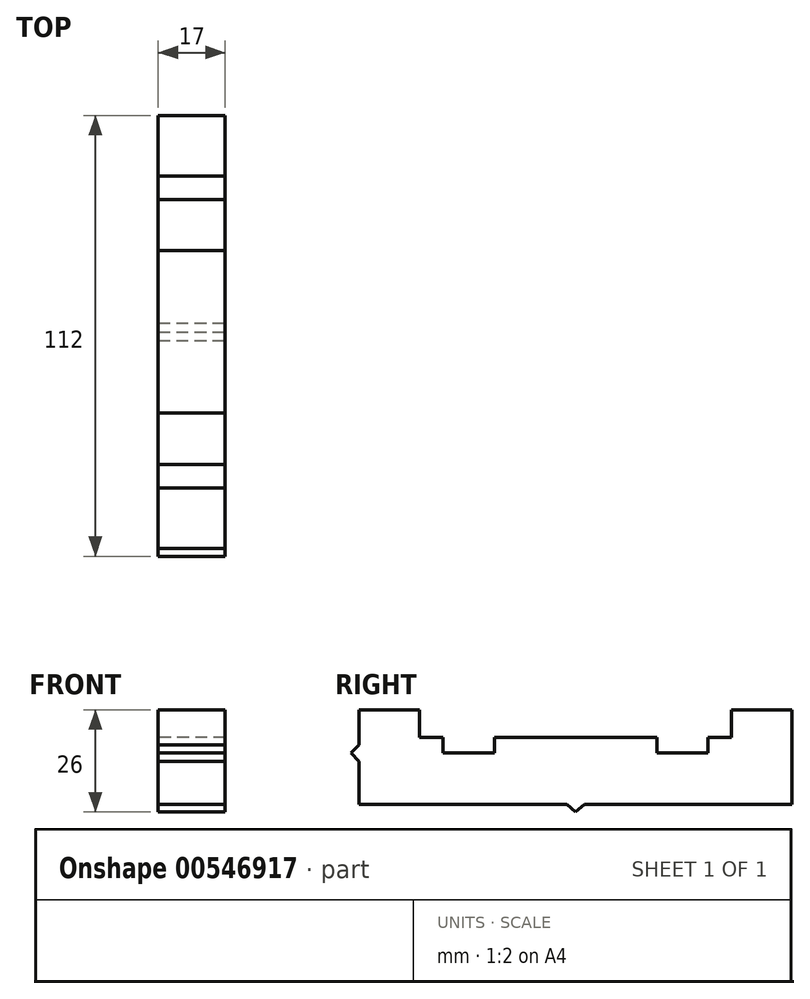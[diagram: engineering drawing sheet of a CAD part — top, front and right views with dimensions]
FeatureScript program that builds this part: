
annotation { "Feature Type Name" : "Feature", "Feature Type Description" : "" }
export const myFeature = defineFeature(function(context is Context, id is Id, definition is map)
    precondition{}
    {
        {
            var Q0;
            Q0=qCreatedBy(makeId("Right.planeOp"),FACE);
            var sketch = newSketch(context, id + "F0", { "sketchPlane" : qUnion([Q0])});
            skLineSegment(sketch, "E0.bottom", {"start": v(0, 0) * mm, "end": v(110, 0) * mm});
            skLineSegment(sketch, "E0.top", {"start": v(0, 24) * mm, "end": v(110, 24) * mm});
            skLineSegment(sketch, "E0.left", {"start": v(0, 0) * mm, "end": v(0, 24) * mm});
            skLineSegment(sketch, "E0.right", {"start": v(110, 0) * mm, "end": v(110, 24) * mm});
            skLineSegment(sketch, "E1.bottom", {"start": v(15.35, 24) * mm, "end": v(94.65, 24) * mm});
            skLineSegment(sketch, "E1.top", {"start": v(15.35, 17) * mm, "end": v(94.65, 17) * mm, "construction": true});
            skLineSegment(sketch, "E1.left", {"start": v(15.35, 24) * mm, "end": v(15.35, 17) * mm});
            skLineSegment(sketch, "E1.right", {"start": v(94.65, 24) * mm, "end": v(94.65, 17) * mm});
            skLineSegment(sketch, "E2", {"start": v(55, 24) * mm, "end": v(55, 0) * mm, "construction": true});
            skLineSegment(sketch, "E3.bottom", {"start": v(21.35, 17) * mm, "end": v(34.35, 17) * mm});
            skLineSegment(sketch, "E3.top", {"start": v(21.35, 13) * mm, "end": v(34.35, 13) * mm});
            skLineSegment(sketch, "E3.left", {"start": v(21.35, 17) * mm, "end": v(21.35, 13) * mm});
            skLineSegment(sketch, "E3.right", {"start": v(34.35, 17) * mm, "end": v(34.35, 13) * mm});
            skLineSegment(sketch, "E4.bottom", {"start": v(88.65, 17) * mm, "end": v(75.65, 17) * mm});
            skLineSegment(sketch, "E4.top", {"start": v(88.65, 13) * mm, "end": v(75.65, 13) * mm});
            skLineSegment(sketch, "E4.left", {"start": v(88.65, 17) * mm, "end": v(88.65, 13) * mm});
            skLineSegment(sketch, "E4.right", {"start": v(75.65, 17) * mm, "end": v(75.65, 13) * mm});
            skLineSegment(sketch, "E5", {"start": v(15.35, 17) * mm, "end": v(21.35, 17) * mm, "construction": true});
            skLineSegment(sketch, "E6", {"start": v(15.35, 17) * mm, "end": v(21.35, 17) * mm});
            skLineSegment(sketch, "E7", {"start": v(34.35, 17) * mm, "end": v(75.65, 17) * mm});
            skLineSegment(sketch, "E8", {"start": v(88.65, 17) * mm, "end": v(94.65, 17) * mm});
            skSolve(sketch);
        }
        {
            var Q0;
            Q0=makeQuery(id+"F0.imprint","IMPRINT",FACE,{"disambiguationData":[TD([[makeQuery(id+"F0.imprint","IMPRINT",EDGE,{"derivedFrom":sQuery(id+"F0.wireOp",EDGE,"E0.bottom")}),1.0]])]});
            extrude(context, id + "F1", {"entities" : qUnion([Q0]), "depth" : 17 * mm, "offsetDistance" : 25 * mm});
        }
        {
            var Q0;
            Q0=makeQuery(id+"F1.opExtrude","CAP_FACE",FACE,{"disambiguationData":[OSD([sQuery(id+"F0.wireOp",EDGE,"E0.bottom"),sQuery(id+"F0.wireOp",EDGE,"E0.top"),sQuery(id+"F0.wireOp",EDGE,"E0.left"),sQuery(id+"F0.wireOp",EDGE,"E0.right"),sQuery(id+"F0.wireOp",EDGE,"E1.left"),sQuery(id+"F0.wireOp",EDGE,"E1.right"),sQuery(id+"F0.wireOp",EDGE,"E3.top"),sQuery(id+"F0.wireOp",EDGE,"E3.left"),sQuery(id+"F0.wireOp",EDGE,"E3.right"),sQuery(id+"F0.wireOp",EDGE,"E4.top"),sQuery(id+"F0.wireOp",EDGE,"E4.left"),sQuery(id+"F0.wireOp",EDGE,"E4.right"),sQuery(id+"F0.wireOp",EDGE,"E6"),sQuery(id+"F0.wireOp",EDGE,"E7"),sQuery(id+"F0.wireOp",EDGE,"E8")])],"isStart":false});
            var sketch = newSketch(context, id + "F2", { "sketchPlane" : qUnion([Q0])});
            skLineSegment(sketch, "E9.0", {"start": v(0, 0) * mm, "end": v(110, 0) * mm});
            skLineSegment(sketch, "E10", {"start": v(55, 0) * mm, "end": v(55, -2) * mm});
            skLineSegment(sketch, "E11", {"start": v(55, -2) * mm, "end": v(52.76, 0) * mm});
            skLineSegment(sketch, "E12", {"start": v(52.76, 0) * mm, "end": v(55, 0) * mm});
            skLineSegment(sketch, "E13.MirrorCS", {"start": v(55, -2) * mm, "end": v(57.24, 0) * mm});
            skLineSegment(sketch, "E14.MirrorCS", {"start": v(57.24, 0) * mm, "end": v(55, 0) * mm});
            skSolve(sketch);
        }
        {
            var Q0;
            Q0=makeQuery(id+"F2.imprint","IMPRINT",FACE,{"disambiguationData":[TD([[makeQuery(id+"F2.imprint","IMPRINT",EDGE,{"derivedFrom":sQuery(id+"F2.wireOp",EDGE,"E10")}),1.0]])]});
            var Q1;
            Q1=makeQuery(id+"F2.imprint","IMPRINT",FACE,{"disambiguationData":[TD([[makeQuery(id+"F2.imprint","IMPRINT",EDGE,{"derivedFrom":sQuery(id+"F2.wireOp",EDGE,"E10")}),-1.0]])]});
            var Q2;
            Q2=makeQuery(id+"F1.opExtrude","CAP_FACE",FACE,{"disambiguationData":[OSD([sQuery(id+"F0.wireOp",EDGE,"E0.bottom"),sQuery(id+"F0.wireOp",EDGE,"E0.top"),sQuery(id+"F0.wireOp",EDGE,"E0.left"),sQuery(id+"F0.wireOp",EDGE,"E0.right"),sQuery(id+"F0.wireOp",EDGE,"E1.left"),sQuery(id+"F0.wireOp",EDGE,"E1.right"),sQuery(id+"F0.wireOp",EDGE,"E3.top"),sQuery(id+"F0.wireOp",EDGE,"E3.left"),sQuery(id+"F0.wireOp",EDGE,"E3.right"),sQuery(id+"F0.wireOp",EDGE,"E4.top"),sQuery(id+"F0.wireOp",EDGE,"E4.left"),sQuery(id+"F0.wireOp",EDGE,"E4.right"),sQuery(id+"F0.wireOp",EDGE,"E6"),sQuery(id+"F0.wireOp",EDGE,"E7"),sQuery(id+"F0.wireOp",EDGE,"E8")])],"isStart":true});
            extrude(context, id + "F3", {"entities" : qUnion([Q0, Q1]), "operationType" : NewBodyOperationType.ADD, "endBound" : BoundingType.UP_TO_SURFACE, "oppositeDirection" : true, "depth" : 25 * mm, "endBoundEntityFace" : qUnion([Q2]), "offsetDistance" : 25 * mm});
        }
        {
            var Q0;
            Q0=makeQuery(id+"F3.boolean.opBoolean","MERGE",FACE,{"derivedFrom":[makeQuery(id+"F1.opExtrude","CAP_FACE",FACE,{"disambiguationData":[OSD([sQuery(id+"F0.wireOp",EDGE,"E0.bottom"),sQuery(id+"F0.wireOp",EDGE,"E0.top"),sQuery(id+"F0.wireOp",EDGE,"E0.left"),sQuery(id+"F0.wireOp",EDGE,"E0.right"),sQuery(id+"F0.wireOp",EDGE,"E1.left"),sQuery(id+"F0.wireOp",EDGE,"E1.right"),sQuery(id+"F0.wireOp",EDGE,"E3.top"),sQuery(id+"F0.wireOp",EDGE,"E3.left"),sQuery(id+"F0.wireOp",EDGE,"E3.right"),sQuery(id+"F0.wireOp",EDGE,"E4.top"),sQuery(id+"F0.wireOp",EDGE,"E4.left"),sQuery(id+"F0.wireOp",EDGE,"E4.right"),sQuery(id+"F0.wireOp",EDGE,"E6"),sQuery(id+"F0.wireOp",EDGE,"E7"),sQuery(id+"F0.wireOp",EDGE,"E8")])],"isStart":false}),makeQuery(id+"F3.opExtrude","CAP_FACE",FACE,{"disambiguationData":[OSD([sQuery(id+"F2.wireOp",EDGE,"E11"),sQuery(id+"F2.wireOp",EDGE,"E12"),sQuery(id+"F2.wireOp",EDGE,"E13.MirrorCS"),sQuery(id+"F2.wireOp",EDGE,"E14.MirrorCS")])],"isStart":true})]});
            var sketch = newSketch(context, id + "F4", { "sketchPlane" : qUnion([Q0])});
            skLineSegment(sketch, "E15.0", {"start": v(21.35, 13) * mm, "end": v(34.35, 13) * mm});
            skLineSegment(sketch, "E16", {"start": v(21.35, 13) * mm, "end": v(0, 13) * mm});
            skLineSegment(sketch, "E17", {"start": v(0, 13) * mm, "end": v(-2, 13) * mm});
            skLineSegment(sketch, "E18", {"start": v(-2, 13) * mm, "end": v(0, 15.12) * mm});
            skLineSegment(sketch, "E19", {"start": v(0, 15.12) * mm, "end": v(0, 13) * mm});
            skLineSegment(sketch, "E20.MirrorCS", {"start": v(-2, 13) * mm, "end": v(0, 10.88) * mm});
            skLineSegment(sketch, "E21.MirrorCS", {"start": v(0, 10.88) * mm, "end": v(0, 13) * mm});
            skSolve(sketch);
        }
        {
            var Q0;
            Q0=makeQuery(id+"F4.imprint","IMPRINT",FACE,{"disambiguationData":[TD([[makeQuery(id+"F4.imprint","IMPRINT",EDGE,{"derivedFrom":sQuery(id+"F4.wireOp",EDGE,"E17")}),1.0]])]});
            var Q1;
            Q1=makeQuery(id+"F4.imprint","IMPRINT",FACE,{"disambiguationData":[TD([[makeQuery(id+"F4.imprint","IMPRINT",EDGE,{"derivedFrom":sQuery(id+"F4.wireOp",EDGE,"E17")}),-1.0]])]});
            var Q2;
            {var subQ0=sQuery(id+"F0.wireOp",EDGE,"E8");var subQ1=sQuery(id+"F0.wireOp",EDGE,"E7");var subQ2=sQuery(id+"F0.wireOp",EDGE,"E6");var subQ3=sQuery(id+"F0.wireOp",EDGE,"E4.right");var subQ4=sQuery(id+"F0.wireOp",EDGE,"E4.left");var subQ5=sQuery(id+"F0.wireOp",EDGE,"E4.top");var subQ6=sQuery(id+"F0.wireOp",EDGE,"E3.right");var subQ7=sQuery(id+"F0.wireOp",EDGE,"E3.left");var subQ8=sQuery(id+"F0.wireOp",EDGE,"E3.top");var subQ9=sQuery(id+"F0.wireOp",EDGE,"E1.right");var subQ10=sQuery(id+"F0.wireOp",EDGE,"E1.left");var subQ11=sQuery(id+"F0.wireOp",EDGE,"E0.right");var subQ12=sQuery(id+"F0.wireOp",EDGE,"E0.left");var subQ13=sQuery(id+"F0.wireOp",EDGE,"E0.top");var subQ14=sQuery(id+"F0.wireOp",EDGE,"E0.bottom");Q2=makeQuery(id+"F3.boolean.opBoolean","MERGE",FACE,{"derivedFrom":[makeQuery(id+"F1.opExtrude","CAP_FACE",FACE,{"disambiguationData":[OSD([subQ14,subQ13,subQ12,subQ11,subQ10,subQ9,subQ8,subQ7,subQ6,subQ5,subQ4,subQ3,subQ2,subQ1,subQ0])],"isStart":true}),makeQuery(id+"F3.opExtrude","CAP_FACE",FACE,{"disambiguationData":[OSD([subQ14,subQ13,subQ12,subQ11,subQ10,subQ9,subQ8,subQ7,subQ6,subQ5,subQ4,subQ3,subQ2,subQ1,subQ0])],"isStart":false})]});}
            extrude(context, id + "F5", {"entities" : qUnion([Q0, Q1]), "operationType" : NewBodyOperationType.ADD, "endBound" : BoundingType.UP_TO_SURFACE, "oppositeDirection" : true, "depth" : 25 * mm, "endBoundEntityFace" : qUnion([Q2]), "offsetDistance" : 25 * mm});
        }
        {
            var Q0;
            {var subQ12=sQuery(id+"F0.wireOp",EDGE,"E0.left");var subQ15=sQuery(id+"F4.wireOp",EDGE,"E18");Q0=makeQuery(id+"F5.boolean.opBoolean","SPLIT",FACE,{"disambiguationData":[TD([makeQuery(id+"F5.opExtrude","SWEPT_FACE",FACE,{"disambiguationData":[OSD([subQ15])]})])],"derivedFrom":makeQuery(id+"F1.opExtrude","SWEPT_FACE",FACE,{"disambiguationData":[OSD([subQ12])]})});}
            var Q1;
            Q1=makeQuery(id+"F1.opExtrude","SWEPT_FACE",FACE,{"disambiguationData":[OSD([sQuery(id+"F0.wireOp",EDGE,"E0.right")])]});
            cPlane(context, id + "F6", {"entities" : qUnion([Q0, Q1]), "cplaneType" : CPlaneType.MID_PLANE, "offset" : 25 * mm, "width" : 150 * mm, "height" : 150 * mm});
        }
    });
